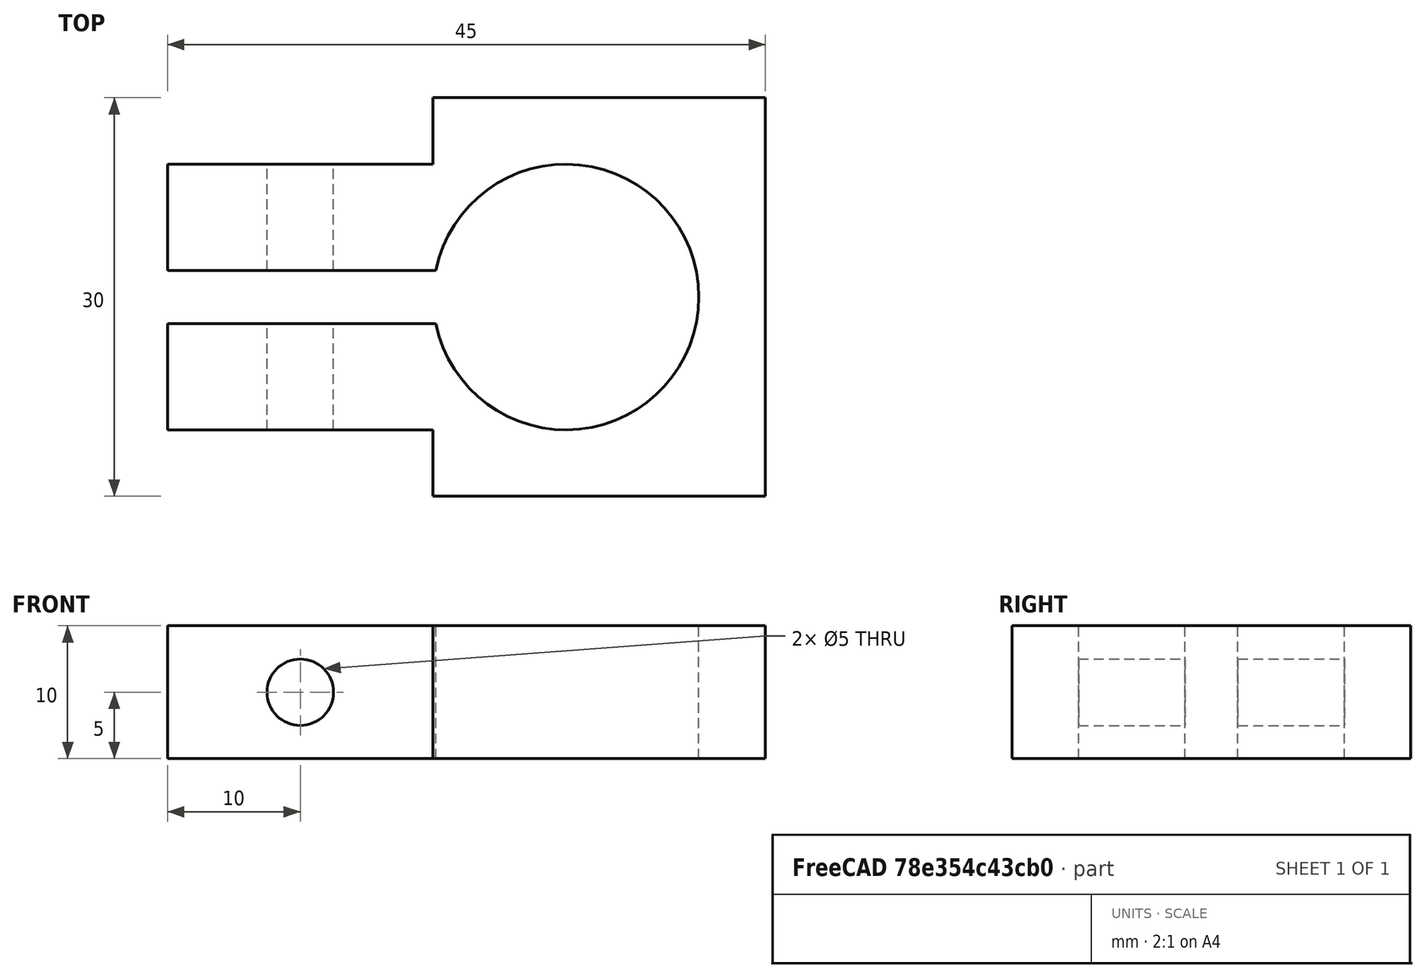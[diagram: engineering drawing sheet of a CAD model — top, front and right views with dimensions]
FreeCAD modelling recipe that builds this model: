
FCSTD DOCUMENT  (FreeCAD 0.17R13522 (Git))
Label: utm-mount
License: All rights reserved
LicenseURL: http://en.wikipedia.org/wiki/All_rights_reserved
objects: Part::Box×4, Part::Cylinder×2, Part::MultiFuse×1, Part::Cut×1
note: 8 computed .brp shape members not serialized (recipe doc carries the construction recipe); baked Part::Feature solids carry a one-line shape summary decoded from their .brp

FEATURE [Part::Cylinder] Cylinder
  Angle = 360
  AttacherType = Attacher::AttachEngine3D
  Height = 10
  Placement = pos=(0,0,-5) rot=(0,0,1;0rad)
  Radius = 10
FEATURE [Part::Box] Box  label="Cube"
  AttacherType = Attacher::AttachEngine3D
  Height = 10
  Length = 45
  Placement = pos=(-30,-15,-5) rot=(0,0,1;0rad)
  Width = 30
FEATURE [Part::Cylinder] Cylinder001
  Angle = 360
  AttacherType = Attacher::AttachEngine3D
  Height = 30
  Placement = pos=(-20,-15,0) rot=(-1,0,0;1.5708rad)
  Radius = 2.5
FEATURE [Part::Box] Box001  label="Cube001"
  AttacherType = Attacher::AttachEngine3D
  Height = 10
  Length = 25
  Placement = pos=(-30,-2,-5) rot=(0,0,1;0rad)
  Width = 4
FEATURE [Part::Box] Box002  label="Cube002"
  AttacherType = Attacher::AttachEngine3D
  Height = 10
  Length = 20
  Placement = pos=(-30,-15,-5) rot=(0,0,1;0rad)
  Width = 5
FEATURE [Part::Box] Box003  label="Cube003"
  AttacherType = Attacher::AttachEngine3D
  Height = 10
  Length = 20
  Placement = pos=(-30,10,-5) rot=(0,0,1;0rad)
  Width = 5
FEATURE [Part::MultiFuse] Fusion  label="Negative Fusion"
  Shapes = -> [Cylinder,Cylinder001,Box001,Box002,Box003]
FEATURE [Part::Cut] Cut
  Base = -> Box
  Tool = -> Fusion
